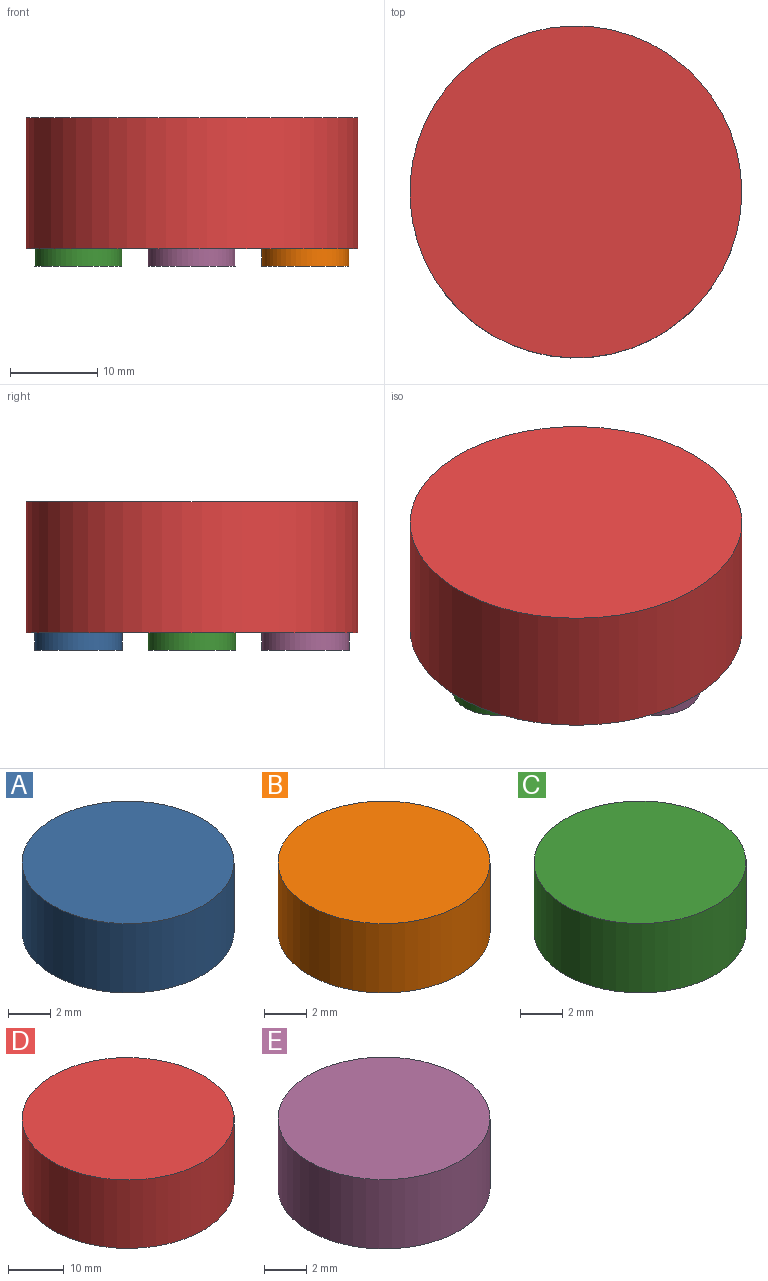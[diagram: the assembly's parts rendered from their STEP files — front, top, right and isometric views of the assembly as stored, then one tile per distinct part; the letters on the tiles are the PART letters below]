
ASSEMBLY  parts=5 mates=4
PART A: 3 faces, bbox 10x10x4 mm
  f0: cylinder r=5mm len=10mm, axis (0,0,1), area 125.7mm2, adj f1,f2
  f1: plane 10x10mm, normal (0,0,-1), area 78.5mm2, adj f0
  f2: plane 10x10mm, normal (0,0,1), area 78.5mm2, adj f0
PART B: 3 faces, bbox 10x10x4 mm
  f0: cylinder r=5mm len=10mm, axis (0,0,1), area 125.7mm2, adj f1,f2
  f1: plane 10x10mm, normal (0,0,-1), area 78.5mm2, adj f0
  f2: plane 10x10mm, normal (0,0,1), area 78.5mm2, adj f0
PART C: 3 faces, bbox 10x10x4 mm
  f0: cylinder r=5mm len=10mm, axis (0,0,-1), area 125.7mm2, adj f1,f2
  f1: plane 10x10mm, normal (0,0,1), area 78.5mm2, adj f0
  f2: plane 10x10mm, normal (0,0,-1), area 78.5mm2, adj f0
PART D: 11 faces, bbox 38x38x15 mm
  f0: cylinder r=5mm len=10mm, axis (0,0,-1), area 62.8mm2, adj f6,f10
  f1: cylinder r=5mm len=10mm, axis (0,0,-1), area 62.8mm2, adj f6,f9
  f2: cylinder r=5mm len=10mm, axis (0,0,-1), area 62.8mm2, adj f6,f8
  f3: cylinder r=5mm len=10mm, axis (0,0,-1), area 62.8mm2, adj f6,f7
  f4: cylinder r=19mm len=38mm, axis (0,0,-1), area 1790.7mm2, adj f5,f6
  f5: plane 38x38mm, normal (0,0,1), area 1134.1mm2, adj f4
  f6: plane 38x38mm, normal (0,0,-1), area 820mm2, adj f0,f1,f2,f3,f4
  f7: plane 10x10mm, normal (0,0,-1), area 78.5mm2, adj f3
  f8: plane 10x10mm, normal (0,0,-1), area 78.5mm2, adj f2
  f9: plane 10x10mm, normal (0,0,-1), area 78.5mm2, adj f1
  f10: plane 10x10mm, normal (0,0,-1), area 78.5mm2, adj f0
PART E: 3 faces, bbox 10x10x4 mm
  f0: cylinder r=5mm len=10mm, axis (0,0,1), area 125.7mm2, adj f1,f2
  f1: plane 10x10mm, normal (0,0,-1), area 78.5mm2, adj f0
  f2: plane 10x10mm, normal (0,0,1), area 78.5mm2, adj f0
PLACE A t=(55.33,-26.93,-9.37)mm
PLACE B t=(63.24,-7.92,-9.37)mm
PLACE C t=(65.14,-19.96,-13.37)mm
PLACE D t=(78.14,-19.96,-11.37)mm
PLACE E t=(31.26,-54.06,-9.37)mm
MATE fastened D.f1 <-> B.f0  axis (0,0,-1) through (91.14,-19.96,-9.37)mm
MATE fastened E.f0 <-> D.f2  axis (0,0,1) through (78.14,-32.96,-9.37)mm
MATE fastened D.f3 <-> A.f0  axis (0,0,-1) through (78.14,-6.96,-9.37)mm
MATE fastened D.f0 <-> C.f0  axis (0,0,-1) through (65.14,-19.96,-9.37)mm
